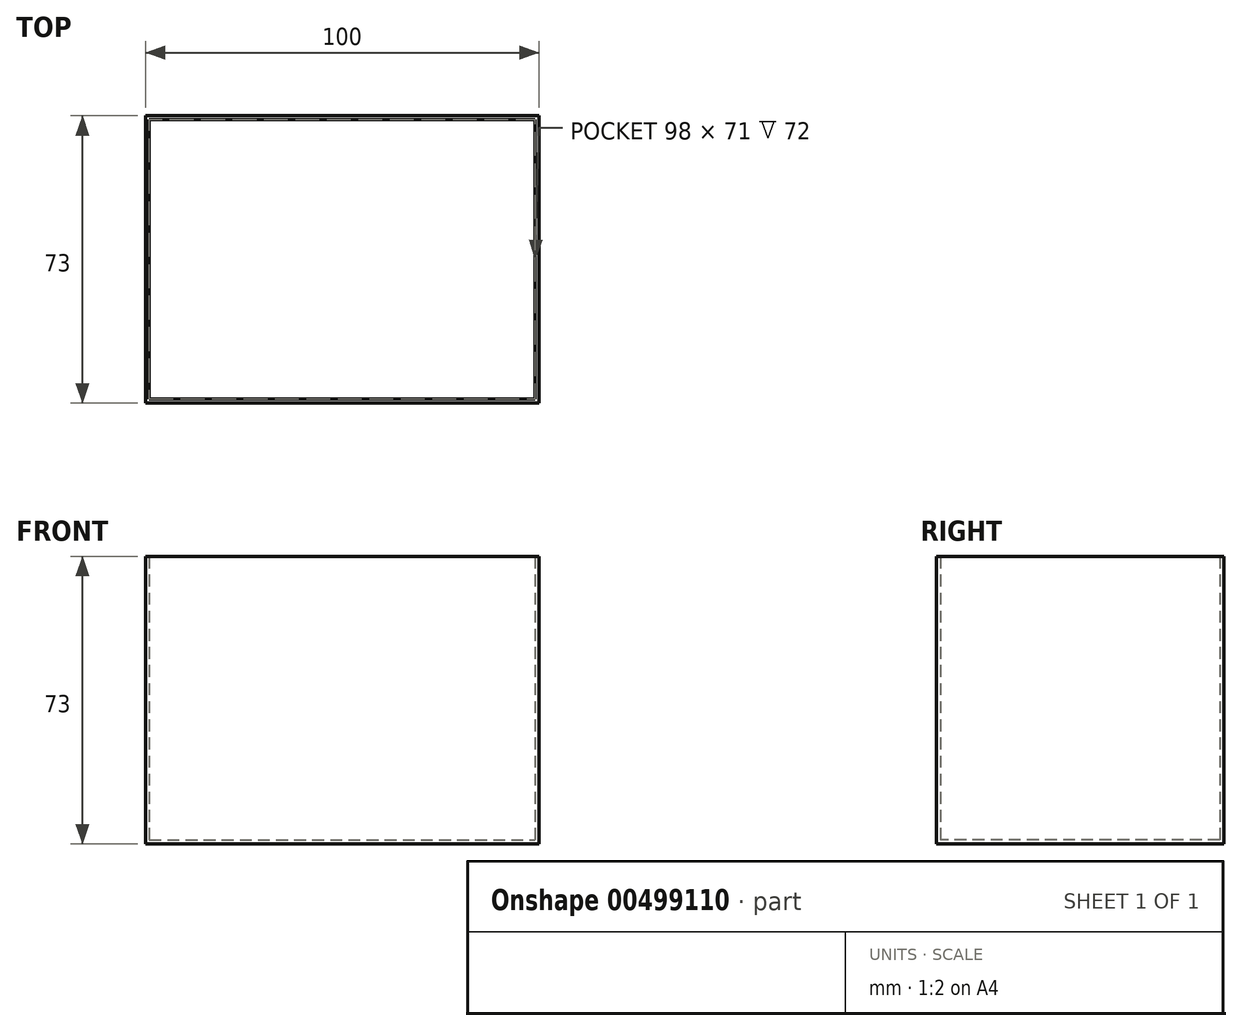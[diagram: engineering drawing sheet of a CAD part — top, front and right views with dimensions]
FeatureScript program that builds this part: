
annotation { "Feature Type Name" : "Feature", "Feature Type Description" : "" }
export const myFeature = defineFeature(function(context is Context, id is Id, definition is map)
    precondition{}
    {
        {
            var Q0;
            Q0=qCreatedBy(makeId("Top.planeOp"),FACE);
            var sketch = newSketch(context, id + "F0", { "sketchPlane" : qUnion([Q0])});
            skPoint(sketch, "E0.middle", {"position": v(0, 0) * mm});
            skLineSegment(sketch, "E1.bottom", {"start": v(-50, 36.5) * mm, "end": v(50, 36.5) * mm});
            skLineSegment(sketch, "E1.top", {"start": v(-50, -36.5) * mm, "end": v(50, -36.5) * mm});
            skLineSegment(sketch, "E1.left", {"start": v(-50, 36.5) * mm, "end": v(-50, -36.5) * mm});
            skLineSegment(sketch, "E1.right", {"start": v(50, 36.5) * mm, "end": v(50, -36.5) * mm});
            skSolve(sketch);
        }
        {
            var Q0;
            Q0=makeQuery(id+"F0.imprint","IMPRINT",FACE,{"disambiguationData":[TD([[makeQuery(id+"F0.imprint","IMPRINT",EDGE,{"derivedFrom":sQuery(id+"F0.wireOp",EDGE,"E1.bottom")}),-1.0]])]});
            extrude(context, id + "F1", {"entities" : qUnion([Q0]), "depth" : 73 * mm});
        }
        {
            var Q0;
            Q0=makeQuery(id+"F1.opExtrude","CAP_FACE",FACE,{"disambiguationData":[OSD([sQuery(id+"F0.wireOp",EDGE,"E1.bottom"),sQuery(id+"F0.wireOp",EDGE,"E1.top"),sQuery(id+"F0.wireOp",EDGE,"E1.left"),sQuery(id+"F0.wireOp",EDGE,"E1.right")])],"isStart":false});
            shell(context, id + "F2", {"entities" : qUnion([Q0]), "thickness" : 1 * mm});
        }
    });
